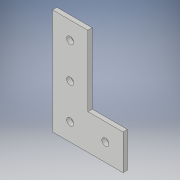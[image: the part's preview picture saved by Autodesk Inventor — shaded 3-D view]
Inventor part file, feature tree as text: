
AUTODESK INVENTOR PART (.ipt)
format: ipt  version: 2018 (Build 220112000, 112)  size: 104,960 bytes
history: native  units: in
note: dims shown in document units (in); Inventor stores cm internally (conversion verified against a paired STEP export)
features: extrude x1, sketch x1
ambient origin geometry x8: Origin, YZ Plane, XZ Plane, XY Plane, X Axis, Y Axis, Z Axis, Center Point
bodies: Solid1 (feature_tree), Body1 (feature_tree)
feature tree (2):
  extrude  "Extrusion1"  Depth=1.0in
  sketch  "Sketch1"  dims[d0=1.0in d1=1.0in d2=1.0in d3=0.0in]
